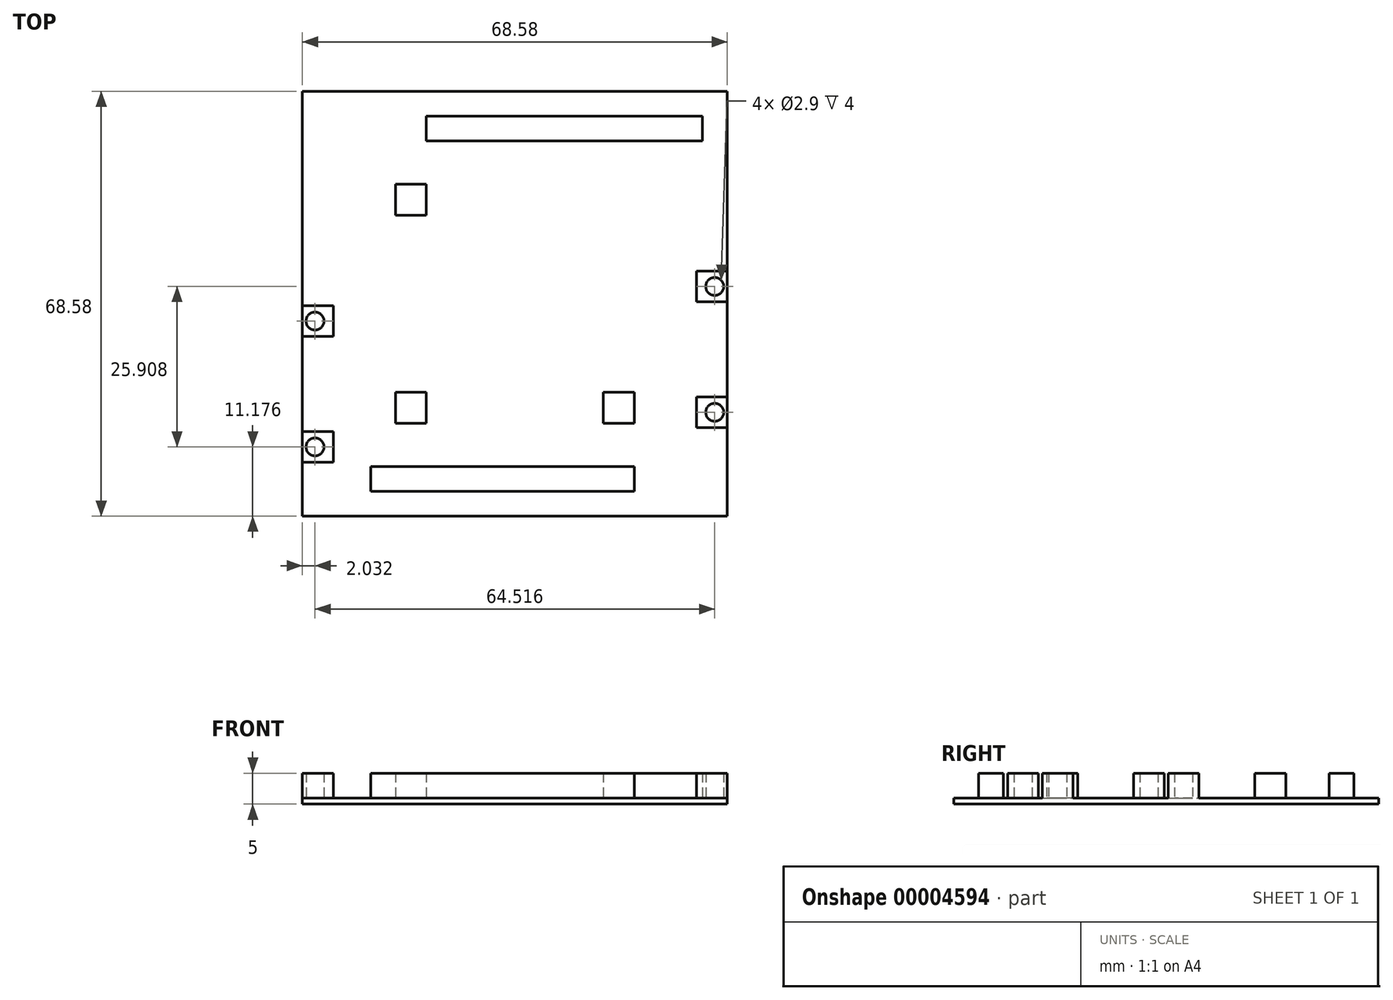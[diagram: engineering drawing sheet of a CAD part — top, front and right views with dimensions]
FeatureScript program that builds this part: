
annotation { "Feature Type Name" : "Feature", "Feature Type Description" : "" }
export const myFeature = defineFeature(function(context is Context, id is Id, definition is map)
    precondition{}
    {
        {
            var Q0;
            Q0=qCreatedBy(makeId("Top.planeOp"),FACE);
            var sketch = newSketch(context, id + "F0", { "sketchPlane" : qUnion([Q0])});
            skLineSegment(sketch, "E0.bottom", {"start": v(0, 0) * mm, "end": v(68.58, 0) * mm});
            skLineSegment(sketch, "E0.top", {"start": v(0, 68.58) * mm, "end": v(68.58, 68.58) * mm});
            skLineSegment(sketch, "E0.left", {"start": v(0, 0) * mm, "end": v(0, 68.58) * mm});
            skLineSegment(sketch, "E0.right", {"start": v(68.58, 0) * mm, "end": v(68.58, 68.58) * mm});
            skSolve(sketch);
        }
        {
            var Q0;
            Q0 = qSketchRegion(id + "F0", true);
            extrude(context, id + "F1", {"entities" : qUnion([Q0]), "depth" : 1 * mm});
        }
        {
            var Q0;
            Q0=makeQuery(id+"F1.opExtrude","CAP_FACE",FACE,{"disambiguationData":[OSD([sQuery(id+"F0.wireOp",EDGE,"E0.bottom"),sQuery(id+"F0.wireOp",EDGE,"E0.top"),sQuery(id+"F0.wireOp",EDGE,"E0.left"),sQuery(id+"F0.wireOp",EDGE,"E0.right")])],"isStart":false});
            var sketch = newSketch(context, id + "F2", { "sketchPlane" : qUnion([Q0])});
            skLineSegment(sketch, "E1.bottom", {"start": v(11, 8) * mm, "end": v(53.58, 8) * mm});
            skLineSegment(sketch, "E1.top", {"start": v(11, 4) * mm, "end": v(53.58, 4) * mm});
            skLineSegment(sketch, "E1.left", {"start": v(11, 8) * mm, "end": v(11, 4) * mm});
            skLineSegment(sketch, "E1.right", {"start": v(53.58, 8) * mm, "end": v(53.58, 4) * mm});
            skLineSegment(sketch, "E2.bottom", {"start": v(15, 20) * mm, "end": v(20, 20) * mm});
            skLineSegment(sketch, "E2.top", {"start": v(15, 15) * mm, "end": v(20, 15) * mm});
            skLineSegment(sketch, "E2.left", {"start": v(15, 20) * mm, "end": v(15, 15) * mm});
            skLineSegment(sketch, "E2.right", {"start": v(20, 20) * mm, "end": v(20, 15) * mm});
            skLineSegment(sketch, "E3.bottom", {"start": v(48.58, 20) * mm, "end": v(53.58, 20) * mm});
            skLineSegment(sketch, "E3.top", {"start": v(48.58, 15) * mm, "end": v(53.58, 15) * mm});
            skLineSegment(sketch, "E3.left", {"start": v(48.58, 20) * mm, "end": v(48.58, 15) * mm});
            skLineSegment(sketch, "E3.right", {"start": v(53.58, 20) * mm, "end": v(53.58, 15) * mm});
            skLineSegment(sketch, "E4.bottom", {"start": v(64.58, 64.58) * mm, "end": v(20, 64.58) * mm});
            skLineSegment(sketch, "E4.top", {"start": v(64.58, 60.58) * mm, "end": v(20, 60.58) * mm});
            skLineSegment(sketch, "E4.left", {"start": v(64.58, 64.58) * mm, "end": v(64.58, 60.58) * mm});
            skLineSegment(sketch, "E4.right", {"start": v(20, 64.58) * mm, "end": v(20, 60.58) * mm});
            skLineSegment(sketch, "E5.bottom", {"start": v(15, 53.58) * mm, "end": v(20, 53.58) * mm});
            skLineSegment(sketch, "E5.top", {"start": v(15, 48.58) * mm, "end": v(20, 48.58) * mm});
            skLineSegment(sketch, "E5.left", {"start": v(15, 53.58) * mm, "end": v(15, 48.58) * mm});
            skLineSegment(sketch, "E5.right", {"start": v(20, 53.58) * mm, "end": v(20, 48.58) * mm});
            skLineSegment(sketch, "E6.bottom", {"start": v(68.58, 14.26) * mm, "end": v(63.58, 14.26) * mm});
            skLineSegment(sketch, "E6.top", {"start": v(68.58, 19.26) * mm, "end": v(63.58, 19.26) * mm});
            skLineSegment(sketch, "E6.left", {"start": v(68.58, 14.26) * mm, "end": v(68.58, 19.26) * mm});
            skLineSegment(sketch, "E6.right", {"start": v(63.58, 14.26) * mm, "end": v(63.58, 19.26) * mm});
            skLineSegment(sketch, "E7.bottom", {"start": v(68.58, 34.58) * mm, "end": v(63.58, 34.58) * mm});
            skLineSegment(sketch, "E7.top", {"start": v(68.58, 39.58) * mm, "end": v(63.58, 39.58) * mm});
            skLineSegment(sketch, "E7.left", {"start": v(68.58, 34.58) * mm, "end": v(68.58, 39.58) * mm});
            skLineSegment(sketch, "E7.right", {"start": v(63.58, 34.58) * mm, "end": v(63.58, 39.58) * mm});
            skLineSegment(sketch, "E8.bottom", {"start": v(0, 8.68) * mm, "end": v(5, 8.68) * mm});
            skLineSegment(sketch, "E8.top", {"start": v(0, 13.68) * mm, "end": v(5, 13.68) * mm});
            skLineSegment(sketch, "E8.left", {"start": v(0, 8.68) * mm, "end": v(0, 13.68) * mm});
            skLineSegment(sketch, "E8.right", {"start": v(5, 8.68) * mm, "end": v(5, 13.68) * mm});
            skLineSegment(sketch, "E9.bottom", {"start": v(0, 34) * mm, "end": v(5, 34) * mm});
            skLineSegment(sketch, "E9.top", {"start": v(0, 29) * mm, "end": v(5, 29) * mm});
            skLineSegment(sketch, "E9.left", {"start": v(0, 34) * mm, "end": v(0, 29) * mm});
            skLineSegment(sketch, "E9.right", {"start": v(5, 34) * mm, "end": v(5, 29) * mm});
            skCircle(sketch, "E10", {"center": v(2.03, 31.5) * mm, "radius": 1.45 * mm});
            skCircle(sketch, "E11", {"center": v(2.03, 11.18) * mm, "radius": 1.45 * mm});
            skCircle(sketch, "E12", {"center": v(66.55, 37.08) * mm, "radius": 1.45 * mm});
            skCircle(sketch, "E13", {"center": v(66.55, 16.76) * mm, "radius": 1.45 * mm});
            skLineSegment(sketch, "E14", {"start": v(0, 31.5) * mm, "end": v(5, 31.5) * mm, "construction": true});
            skLineSegment(sketch, "E15", {"start": v(0, 11.18) * mm, "end": v(5, 11.18) * mm, "construction": true});
            skLineSegment(sketch, "E16", {"start": v(63.58, 37.08) * mm, "end": v(68.58, 37.08) * mm, "construction": true});
            skLineSegment(sketch, "E17", {"start": v(63.58, 16.76) * mm, "end": v(68.58, 16.76) * mm, "construction": true});
            skSolve(sketch);
        }
        {
            var Q0;
            Q0=makeQuery(id+"F2.imprint","IMPRINT",FACE,{"disambiguationData":[TD([[makeQuery(id+"F2.imprint","IMPRINT",EDGE,{"derivedFrom":sQuery(id+"F2.wireOp",EDGE,"E4.bottom")}),1.0]])]});
            var Q1;
            Q1=makeQuery(id+"F2.imprint","IMPRINT",FACE,{"disambiguationData":[TD([[makeQuery(id+"F2.imprint","IMPRINT",EDGE,{"derivedFrom":sQuery(id+"F2.wireOp",EDGE,"E3.bottom")}),-1.0]])]});
            var Q2;
            Q2=makeQuery(id+"F2.imprint","IMPRINT",FACE,{"disambiguationData":[TD([[makeQuery(id+"F2.imprint","IMPRINT",EDGE,{"derivedFrom":sQuery(id+"F2.wireOp",EDGE,"E1.bottom")}),-1.0]])]});
            var Q3;
            Q3=makeQuery(id+"F2.imprint","IMPRINT",FACE,{"disambiguationData":[TD([[makeQuery(id+"F2.imprint","IMPRINT",EDGE,{"derivedFrom":sQuery(id+"F2.wireOp",EDGE,"E2.bottom")}),-1.0]])]});
            var Q4;
            Q4=makeQuery(id+"F2.imprint","IMPRINT",FACE,{"disambiguationData":[TD([[makeQuery(id+"F2.imprint","IMPRINT",EDGE,{"derivedFrom":sQuery(id+"F2.wireOp",EDGE,"E5.bottom")}),-1.0]])]});
            var Q5;
            Q5=makeQuery(id+"F2.imprint","IMPRINT",FACE,{"disambiguationData":[TD([[makeQuery(id+"F2.imprint","IMPRINT",EDGE,{"derivedFrom":sQuery(id+"F2.wireOp",EDGE,"E9.bottom")}),-1.0]])]});
            var Q6;
            Q6=makeQuery(id+"F2.imprint","IMPRINT",FACE,{"disambiguationData":[TD([[makeQuery(id+"F2.imprint","IMPRINT",EDGE,{"derivedFrom":sQuery(id+"F2.wireOp",EDGE,"E8.bottom")}),1.0]])]});
            var Q7;
            Q7=makeQuery(id+"F2.imprint","IMPRINT",FACE,{"disambiguationData":[TD([[makeQuery(id+"F2.imprint","IMPRINT",EDGE,{"derivedFrom":sQuery(id+"F2.wireOp",EDGE,"E7.bottom")}),-1.0]])]});
            var Q8;
            Q8=makeQuery(id+"F2.imprint","IMPRINT",FACE,{"disambiguationData":[TD([[makeQuery(id+"F2.imprint","IMPRINT",EDGE,{"derivedFrom":sQuery(id+"F2.wireOp",EDGE,"E6.bottom")}),-1.0]])]});
            extrude(context, id + "F3", {"entities" : qUnion([Q0, Q1, Q2, Q3, Q4, Q5, Q6, Q7, Q8]), "operationType" : NewBodyOperationType.ADD, "depth" : 4 * mm});
        }
    });
